# Revit family: 11583,002
name_source: partatom
category: Plumbing Fixtures
units: mm (PartAtom-declared; Revit-internal decimal feet)

## family parameters
Always vertical = Yes
Cut with Voids When Loaded = No
Enable Cutting in Views = Yes
Maintain Annotation Orientation = No
OmniClass Number = 23.45.30.14.11
OmniClass Title = Commercial Dishwashers
Part Type = Normal
Room Calculation Point = No
Round Connector Dimension = Use Diameter
Shared = No
Work Plane-Based = No

## types (1)
- Standard
    CW Connection = No
    Connector_5_Diameter = 22 mm  [stored 0.0721785 ft]
    Connector_6_Diameter = 22 mm  [stored 0.0721785 ft]
    Connector_8_Diameter = 54 mm
    Default Elevation = 0 mm  [stored 0 ft]
    Description = Rack conveyor dishwasher
    HW Connection = No
    Manufacturer = Wexiödisk AB
    Model = WD-241/243
    URL = www.wexiodisk.com
    Vent Connection = No
    Waste Connection = No

note: [stored X ft] marks values corroborated as IEEE doubles in the binary element streams (Revit-internal decimal feet)

## geometry (parser evidence)
native form markers: Sweep x3
no freeform markers — native parametric forms only
